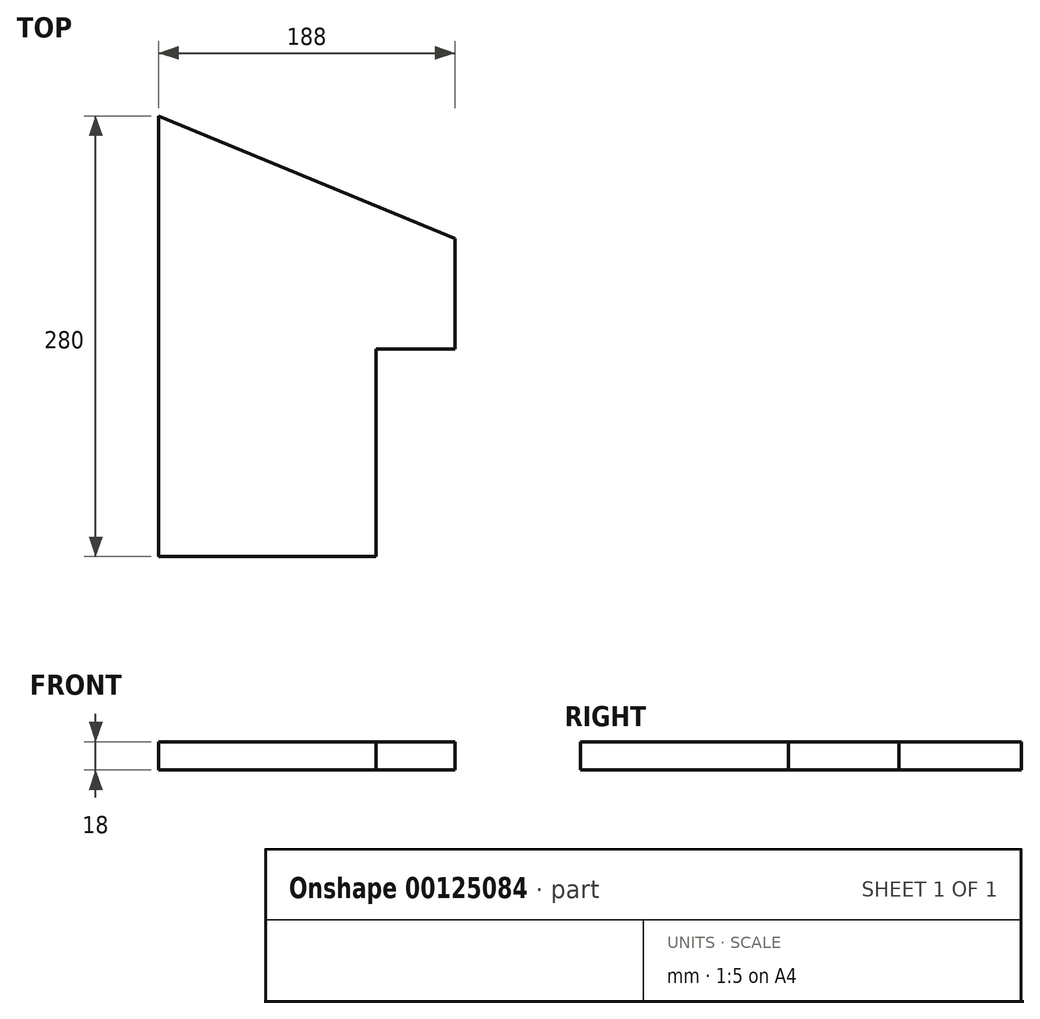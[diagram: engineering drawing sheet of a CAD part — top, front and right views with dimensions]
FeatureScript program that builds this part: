
annotation { "Feature Type Name" : "Feature", "Feature Type Description" : "" }
export const myFeature = defineFeature(function(context is Context, id is Id, definition is map)
    precondition{}
    {
        {
            var Q0;
            Q0=qCreatedBy(makeId("Top.planeOp"),FACE);
            var sketch = newSketch(context, id + "F0", { "sketchPlane" : qUnion([Q0])});
            skLineSegment(sketch, "E0", {"start": v(0, 0) * mm, "end": v(0, 280) * mm});
            skLineSegment(sketch, "E1", {"start": v(0, 280) * mm, "end": v(188, 202) * mm});
            skLineSegment(sketch, "E2", {"start": v(188, 202) * mm, "end": v(188, 132) * mm});
            skLineSegment(sketch, "E3", {"start": v(188, 132) * mm, "end": v(138, 132) * mm});
            skLineSegment(sketch, "E4", {"start": v(138, 132) * mm, "end": v(138, 0) * mm});
            skLineSegment(sketch, "E5", {"start": v(138, 0) * mm, "end": v(0, 0) * mm});
            skSolve(sketch);
        }
        {
            var Q0;
            Q0=makeQuery(id+"F0.imprint","IMPRINT",FACE,{"disambiguationData":[TD([[makeQuery(id+"F0.imprint","IMPRINT",EDGE,{"derivedFrom":sQuery(id+"F0.wireOp",EDGE,"E0")}),-1.0]])]});
            extrude(context, id + "F1", {"entities" : qUnion([Q0]), "depth" : 18 * mm});
        }
    });
